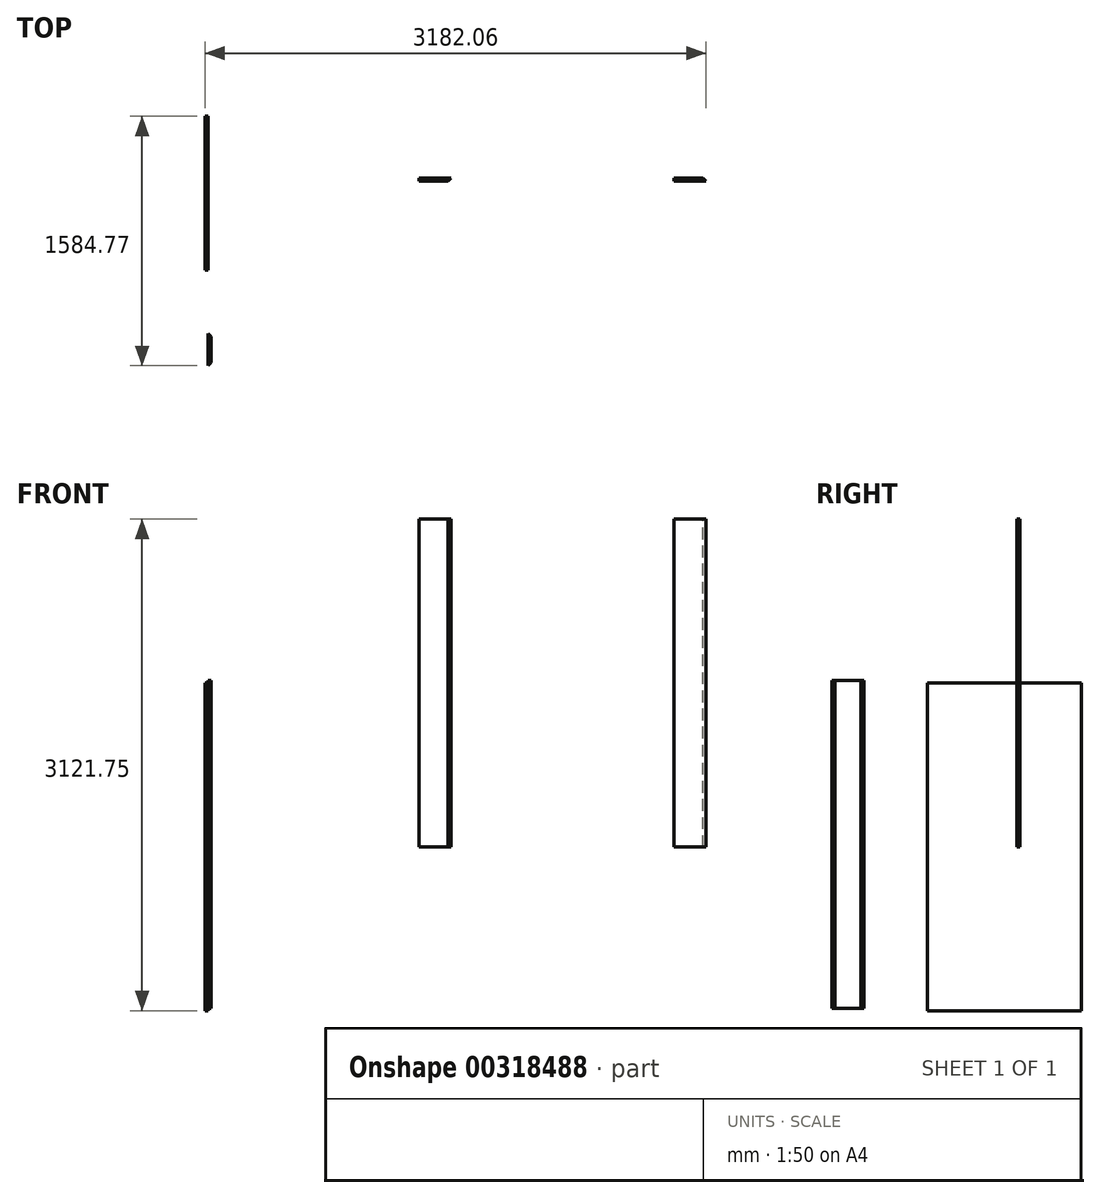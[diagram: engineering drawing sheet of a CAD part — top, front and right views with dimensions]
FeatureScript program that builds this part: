
annotation { "Feature Type Name" : "Feature", "Feature Type Description" : "" }
export const myFeature = defineFeature(function(context is Context, id is Id, definition is map)
    precondition{}
    {
        {
            var Q0;
            Q0=qCreatedBy(makeId("Right.planeOp"),FACE);
            var sketch = newSketch(context, id + "F0", { "sketchPlane" : qUnion([Q0])});
            skLineSegment(sketch, "E0.bottom", {"start": v(-585.96, 1043.85) * mm, "end": v(391.94, 1043.85) * mm});
            skLineSegment(sketch, "E0.top", {"start": v(-585.96, -1038.95) * mm, "end": v(391.94, -1038.95) * mm});
            skLineSegment(sketch, "E0.left", {"start": v(-585.96, 1043.85) * mm, "end": v(-585.96, -1038.95) * mm});
            skLineSegment(sketch, "E0.right", {"start": v(391.94, 1043.85) * mm, "end": v(391.94, -1038.95) * mm});
            skSolve(sketch);
        }
        {
            var Q0;
            Q0 = qSketchRegion(id + "F0", true);
            extrude(context, id + "F1", {"entities" : qUnion([Q0]), "depth" : 19.05 * mm});
        }
        {
            var Q0;
            Q0=qCreatedBy(makeId("Front.planeOp"),FACE);
            var sketch = newSketch(context, id + "F2", { "sketchPlane" : qUnion([Q0])});
            skLineSegment(sketch, "E1.bottom", {"start": v(3182.06, 2082.8) * mm, "end": v(2978.86, 2082.8) * mm});
            skLineSegment(sketch, "E1.top", {"start": v(3182.06, 0) * mm, "end": v(2978.86, 0) * mm});
            skLineSegment(sketch, "E1.left", {"start": v(3182.06, 2082.8) * mm, "end": v(3182.06, 0) * mm});
            skLineSegment(sketch, "E1.right", {"start": v(2978.86, 2082.8) * mm, "end": v(2978.86, 0) * mm});
            skSolve(sketch);
        }
        {
            var Q0;
            Q0 = qSketchRegion(id + "F2", true);
            extrude(context, id + "F3", {"entities" : qUnion([Q0]), "depth" : 19.05 * mm});
        }
        {
            var Q0;
            Q0=makeQuery(id+"F3.opExtrude","SWEPT_FACE",FACE,{"disambiguationData":[OSD([sQuery(id+"F2.wireOp",EDGE,"E1.bottom")])]});
            var sketch = newSketch(context, id + "F4", { "sketchPlane" : qUnion([Q0])});
            skLineSegment(sketch, "E2.0", {"start": v(3163.01, -19.05) * mm, "end": v(3163.01, 0) * mm, "construction": true});
            skLineSegment(sketch, "E3", {"start": v(3182.06, -19.05) * mm, "end": v(3163.01, 0) * mm});
            skSolve(sketch);
        }
        {
            var Q0;
            {var subQ0=sQuery(id+"F4.wireOp",EDGE,"E3");Q0=makeQuery(id+"F4.imprint","IMPRINT",FACE,{"disambiguationData":[TD([[makeQuery(id+"F4.imprint","IMPRINT",EDGE,{"derivedFrom":subQ0}),-1.0]])]});}
            extrude(context, id + "F5", {"entities" : qUnion([Q0]), "operationType" : NewBodyOperationType.REMOVE, "oppositeDirection" : true, "depth" : 2082.8 * mm});
        }
        {
            var Q0;
            Q0=makeQuery(id+"F3.opExtrude","CAP_FACE",FACE,{"disambiguationData":[OSD([sQuery(id+"F2.wireOp",EDGE,"E1.bottom"),sQuery(id+"F2.wireOp",EDGE,"E1.top"),sQuery(id+"F2.wireOp",EDGE,"E1.left"),sQuery(id+"F2.wireOp",EDGE,"E1.right")])],"isStart":false});
            var sketch = newSketch(context, id + "F6", { "sketchPlane" : qUnion([Q0])});
            skLineSegment(sketch, "E4.bottom", {"start": v(1357.99, 2082.8) * mm, "end": v(1561.19, 2082.8) * mm});
            skLineSegment(sketch, "E4.top", {"start": v(1357.99, 0) * mm, "end": v(1561.19, 0) * mm});
            skLineSegment(sketch, "E4.left", {"start": v(1357.99, 2082.8) * mm, "end": v(1357.99, 0) * mm});
            skLineSegment(sketch, "E4.right", {"start": v(1561.19, 2082.8) * mm, "end": v(1561.19, 0) * mm});
            skSolve(sketch);
        }
        {
            var Q0;
            Q0 = qSketchRegion(id + "F6", true);
            extrude(context, id + "F7", {"entities" : qUnion([Q0]), "oppositeDirection" : true, "depth" : 19.05 * mm});
        }
        {
            var Q0;
            Q0=makeQuery(id+"F7.opExtrude","SWEPT_FACE",FACE,{"disambiguationData":[OSD([sQuery(id+"F6.wireOp",EDGE,"E4.bottom")])]});
            var sketch = newSketch(context, id + "F8", { "sketchPlane" : qUnion([Q0])});
            skLineSegment(sketch, "E5.0", {"start": v(1542.14, 0) * mm, "end": v(1542.14, -19.05) * mm, "construction": true});
            skLineSegment(sketch, "E6", {"start": v(1542.14, -19.05) * mm, "end": v(1561.19, 0) * mm});
            skSolve(sketch);
        }
        {
            var Q0;
            {var subQ0=sQuery(id+"F8.wireOp",EDGE,"E6");Q0=makeQuery(id+"F8.imprint","IMPRINT",FACE,{"disambiguationData":[TD([[makeQuery(id+"F8.imprint","IMPRINT",EDGE,{"derivedFrom":subQ0}),-1.0]])]});}
            extrude(context, id + "F9", {"entities" : qUnion([Q0]), "operationType" : NewBodyOperationType.REMOVE, "oppositeDirection" : true, "depth" : 2082.8 * mm});
        }
        {
            var Q0;
            Q0=makeQuery(id+"F1.opExtrude","CAP_FACE",FACE,{"disambiguationData":[OSD([sQuery(id+"F0.wireOp",EDGE,"E0.bottom"),sQuery(id+"F0.wireOp",EDGE,"E0.top"),sQuery(id+"F0.wireOp",EDGE,"E0.left"),sQuery(id+"F0.wireOp",EDGE,"E0.right")])],"isStart":false});
            var sketch = newSketch(context, id + "F10", { "sketchPlane" : qUnion([Q0])});
            skLineSegment(sketch, "E7.bottom", {"start": v(-1192.83, 1057.66) * mm, "end": v(-989.63, 1057.66) * mm});
            skLineSegment(sketch, "E7.top", {"start": v(-1192.83, -1025.14) * mm, "end": v(-989.63, -1025.14) * mm});
            skLineSegment(sketch, "E7.left", {"start": v(-1192.83, 1057.66) * mm, "end": v(-1192.83, -1025.14) * mm});
            skLineSegment(sketch, "E7.right", {"start": v(-989.63, 1057.66) * mm, "end": v(-989.63, -1025.14) * mm});
            skSolve(sketch);
        }
        {
            var Q0;
            Q0=makeQuery(id+"F10.imprint","IMPRINT",FACE,{"disambiguationData":[TD([[makeQuery(id+"F10.imprint","IMPRINT",EDGE,{"derivedFrom":sQuery(id+"F10.wireOp",EDGE,"E7.bottom")}),-1.0]])]});
            extrude(context, id + "F11", {"entities" : qUnion([Q0]), "depth" : 19.05 * mm});
        }
        {
            var Q0;
            Q0=makeQuery(id+"F11.opExtrude","SWEPT_FACE",FACE,{"disambiguationData":[OSD([sQuery(id+"F10.wireOp",EDGE,"E7.bottom")])]});
            var sketch = newSketch(context, id + "F12", { "sketchPlane" : qUnion([Q0])});
            skLineSegment(sketch, "E8.0", {"start": v(38.1, -1173.78) * mm, "end": v(19.05, -1173.78) * mm, "construction": true});
            skLineSegment(sketch, "E9.0", {"start": v(38.1, -1008.68) * mm, "end": v(19.05, -1008.68) * mm, "construction": true});
            skLineSegment(sketch, "E10", {"start": v(38.1, -1173.78) * mm, "end": v(19.05, -1192.83) * mm});
            skLineSegment(sketch, "E11", {"start": v(38.1, -1008.68) * mm, "end": v(19.05, -989.63) * mm});
            skSolve(sketch);
        }
        {
            var Q0;
            {var subQ0=sQuery(id+"F12.wireOp",EDGE,"E10");Q0=makeQuery(id+"F12.imprint","IMPRINT",FACE,{"disambiguationData":[TD([[makeQuery(id+"F12.imprint","IMPRINT",EDGE,{"derivedFrom":subQ0}),1.0]])]});}
            var Q1;
            {var subQ0=sQuery(id+"F12.wireOp",EDGE,"E11");Q1=makeQuery(id+"F12.imprint","IMPRINT",FACE,{"disambiguationData":[TD([[makeQuery(id+"F12.imprint","IMPRINT",EDGE,{"derivedFrom":subQ0}),-1.0]])]});}
            extrude(context, id + "F13", {"entities" : qUnion([Q0, Q1]), "operationType" : NewBodyOperationType.REMOVE, "oppositeDirection" : true, "depth" : 2082.8 * mm});
        }
    });
